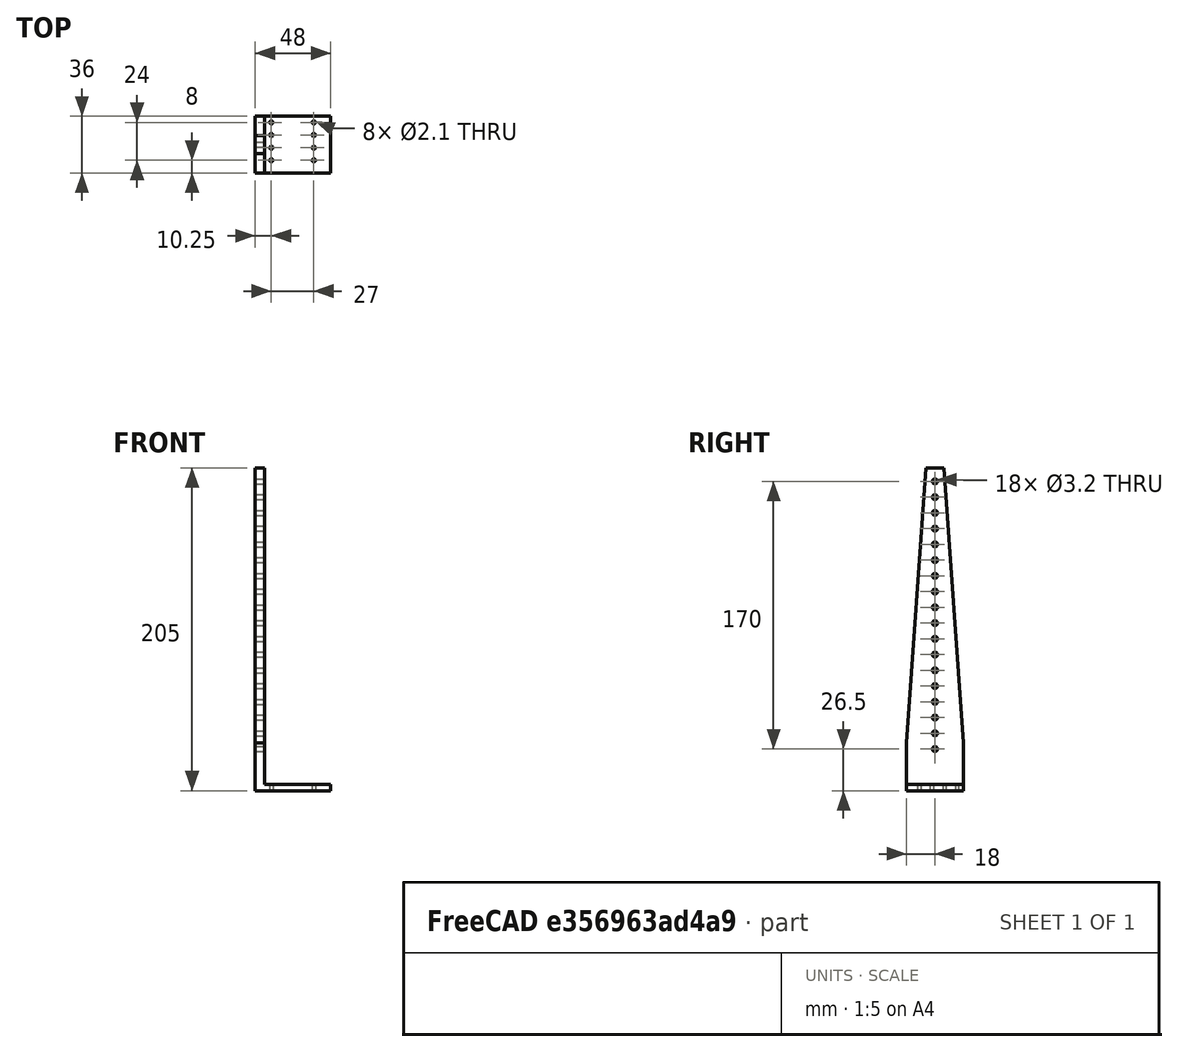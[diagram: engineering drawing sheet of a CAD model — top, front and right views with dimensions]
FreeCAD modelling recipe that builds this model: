
FCSTD DOCUMENT  (FreeCAD 0.15R4671 (Git))
Label: weight_frame_elbow
License: All rights reserved
LicenseURL: http://en.wikipedia.org/wiki/All_rights_reserved
objects: Part::Cylinder×27, Part::MultiFuse×6, Part::Box×3, Part::Mirroring×1, Part::Cut×1
note: 38 computed .brp shape members not serialized (recipe doc carries the construction recipe); baked Part::Feature solids carry a one-line shape summary decoded from their .brp

FEATURE [Part::Box] Box  label="Cube"
  Height = 4
  Length = 48
  Width = 36
FEATURE [Part::Box] Box001  label="Cube001"
  Height = 205
  Length = 6
  Width = 36
FEATURE [Part::Box] Box002  label="Cube002"
  Height = 250
  Length = 10
  Placement = pos=(-3,-54,-25) rot=(-1,0,0;0.069813rad)
  Width = 50
FEATURE [Part::MultiFuse] Fusion001
  Shapes = -> [Box,Box001]
FEATURE [Part::Cylinder] Cylinder
  Angle = 360
  Height = 10
  Placement = pos=(0,25,26.5) rot=(0,1,0;1.5708rad)
  Radius = 1.6
FEATURE [Part::Cylinder] Cylinder001
  Angle = 360
  Height = 10
  Placement = pos=(0,25,36.5) rot=(0,1,0;1.5708rad)
  Radius = 1.6
FEATURE [Part::Cylinder] Cylinder002
  Angle = 360
  Height = 10
  Placement = pos=(0,25,46.5) rot=(0,1,0;1.5708rad)
  Radius = 1.6
FEATURE [Part::Cylinder] Cylinder003
  Angle = 360
  Height = 10
  Placement = pos=(0,25,46.5) rot=(0,1,0;1.5708rad)
  Radius = 1.6
FEATURE [Part::Cylinder] Cylinder004
  Angle = 360
  Height = 10
  Placement = pos=(0,25,56.5) rot=(0,1,0;1.5708rad)
  Radius = 1.6
FEATURE [Part::Cylinder] Cylinder005
  Angle = 360
  Height = 10
  Placement = pos=(0,25,66.5) rot=(0,1,0;1.5708rad)
  Radius = 1.6
FEATURE [Part::Cylinder] Cylinder006
  Angle = 360
  Height = 10
  Placement = pos=(0,25,76.5) rot=(0,1,0;1.5708rad)
  Radius = 1.6
FEATURE [Part::Cylinder] Cylinder007
  Angle = 360
  Height = 10
  Placement = pos=(0,25,86.5) rot=(0,1,0;1.5708rad)
  Radius = 1.6
FEATURE [Part::Cylinder] Cylinder008
  Angle = 360
  Height = 10
  Placement = pos=(0,25,96.5) rot=(0,1,0;1.5708rad)
  Radius = 1.6
FEATURE [Part::Cylinder] Cylinder009
  Angle = 360
  Height = 10
  Placement = pos=(0,25,106.5) rot=(0,1,0;1.5708rad)
  Radius = 1.6
FEATURE [Part::Cylinder] Cylinder010
  Angle = 360
  Height = 10
  Placement = pos=(0,25,116.5) rot=(0,1,0;1.5708rad)
  Radius = 1.6
FEATURE [Part::Cylinder] Cylinder011
  Angle = 360
  Height = 10
  Placement = pos=(0,25,126.5) rot=(0,1,0;1.5708rad)
  Radius = 1.6
FEATURE [Part::Cylinder] Cylinder012
  Angle = 360
  Height = 10
  Placement = pos=(0,25,136.5) rot=(0,1,0;1.5708rad)
  Radius = 1.6
FEATURE [Part::Cylinder] Cylinder013
  Angle = 360
  Height = 10
  Placement = pos=(0,25,146.5) rot=(0,1,0;1.5708rad)
  Radius = 1.6
FEATURE [Part::Cylinder] Cylinder014
  Angle = 360
  Height = 10
  Placement = pos=(0,25,156.5) rot=(0,1,0;1.5708rad)
  Radius = 1.6
FEATURE [Part::Cylinder] Cylinder015
  Angle = 360
  Height = 10
  Placement = pos=(0,25,166.5) rot=(0,1,0;1.5708rad)
  Radius = 1.6
FEATURE [Part::Cylinder] Cylinder016
  Angle = 360
  Height = 10
  Placement = pos=(0,25,176.5) rot=(0,1,0;1.5708rad)
  Radius = 1.6
FEATURE [Part::Cylinder] Cylinder017
  Angle = 360
  Height = 10
  Placement = pos=(0,25,186.5) rot=(0,1,0;1.5708rad)
  Radius = 1.6
FEATURE [Part::Cylinder] Cylinder018
  Angle = 360
  Height = 10
  Placement = pos=(0,25,196.5) rot=(0,1,0;1.5708rad)
  Radius = 1.6
FEATURE [Part::MultiFuse] Fusion002
  Placement = pos=(0,-7,0) rot=(0,0,1;0rad)
  Shapes = -> [Cylinder,Cylinder005,Cylinder012,Cylinder014,Cylinder003,Cylinder001,Cylinder008,Cylinder009,Cylinder002,Cylinder013,Cylinder011,Cylinder006,Cylinder016,Cylinder018,Cylinder015,Cylinder017,Cylinder010,Cylinder007,Cylinder004]
FEATURE [Part::Cylinder] Cylinder019
  Angle = 360
  Height = 10
  Placement = pos=(-4,16,10.25) rot=(0,1,0;1.5708rad)
  Radius = 1.05
FEATURE [Part::Cylinder] Cylinder020
  Angle = 360
  Height = 10
  Placement = pos=(-4,24,10.25) rot=(0,1,0;1.5708rad)
  Radius = 1.05
FEATURE [Part::Cylinder] Cylinder021
  Angle = 360
  Height = 10
  Placement = pos=(-4,32,10.25) rot=(0,1,0;1.5708rad)
  Radius = 1.05
FEATURE [Part::Cylinder] Cylinder022
  Angle = 360
  Height = 10
  Placement = pos=(-4,8,10.25) rot=(0,1,0;1.5708rad)
  Radius = 1.05
FEATURE [Part::MultiFuse] Fusion003
  Placement = pos=(0,0,0) rot=(0,1,0;1.5708rad)
  Shapes = -> [Cylinder019,Cylinder021,Cylinder020,Cylinder022]
FEATURE [Part::Cylinder] Cylinder023
  Angle = 360
  Height = 10
  Placement = pos=(-4,16,10.25) rot=(0,1,0;1.5708rad)
  Radius = 1.05
FEATURE [Part::Cylinder] Cylinder024
  Angle = 360
  Height = 10
  Placement = pos=(-4,24,10.25) rot=(0,1,0;1.5708rad)
  Radius = 1.05
FEATURE [Part::Cylinder] Cylinder025
  Angle = 360
  Height = 10
  Placement = pos=(-4,32,10.25) rot=(0,1,0;1.5708rad)
  Radius = 1.05
FEATURE [Part::Cylinder] Cylinder026
  Angle = 360
  Height = 10
  Placement = pos=(-4,8,10.25) rot=(0,1,0;1.5708rad)
  Radius = 1.05
FEATURE [Part::MultiFuse] Fusion004
  Placement = pos=(27,0,0) rot=(0,1,0;1.5708rad)
  Shapes = -> [Cylinder023,Cylinder025,Cylinder024,Cylinder026]
FEATURE [Part::Mirroring] Part__Mirroring  label="Cube002 (Mirror #1)"
  Base = (0,18,0)
  Normal = (0,1,0)
  Source = -> Box002
FEATURE [Part::MultiFuse] Fusion
  Shapes = -> [Box002,Part__Mirroring]
FEATURE [Part::MultiFuse] Fusion005
  Shapes = -> [Fusion002,Fusion003,Fusion004,Fusion]
FEATURE [Part::Cut] Cut
  Base = -> Fusion001
  Tool = -> Fusion005
